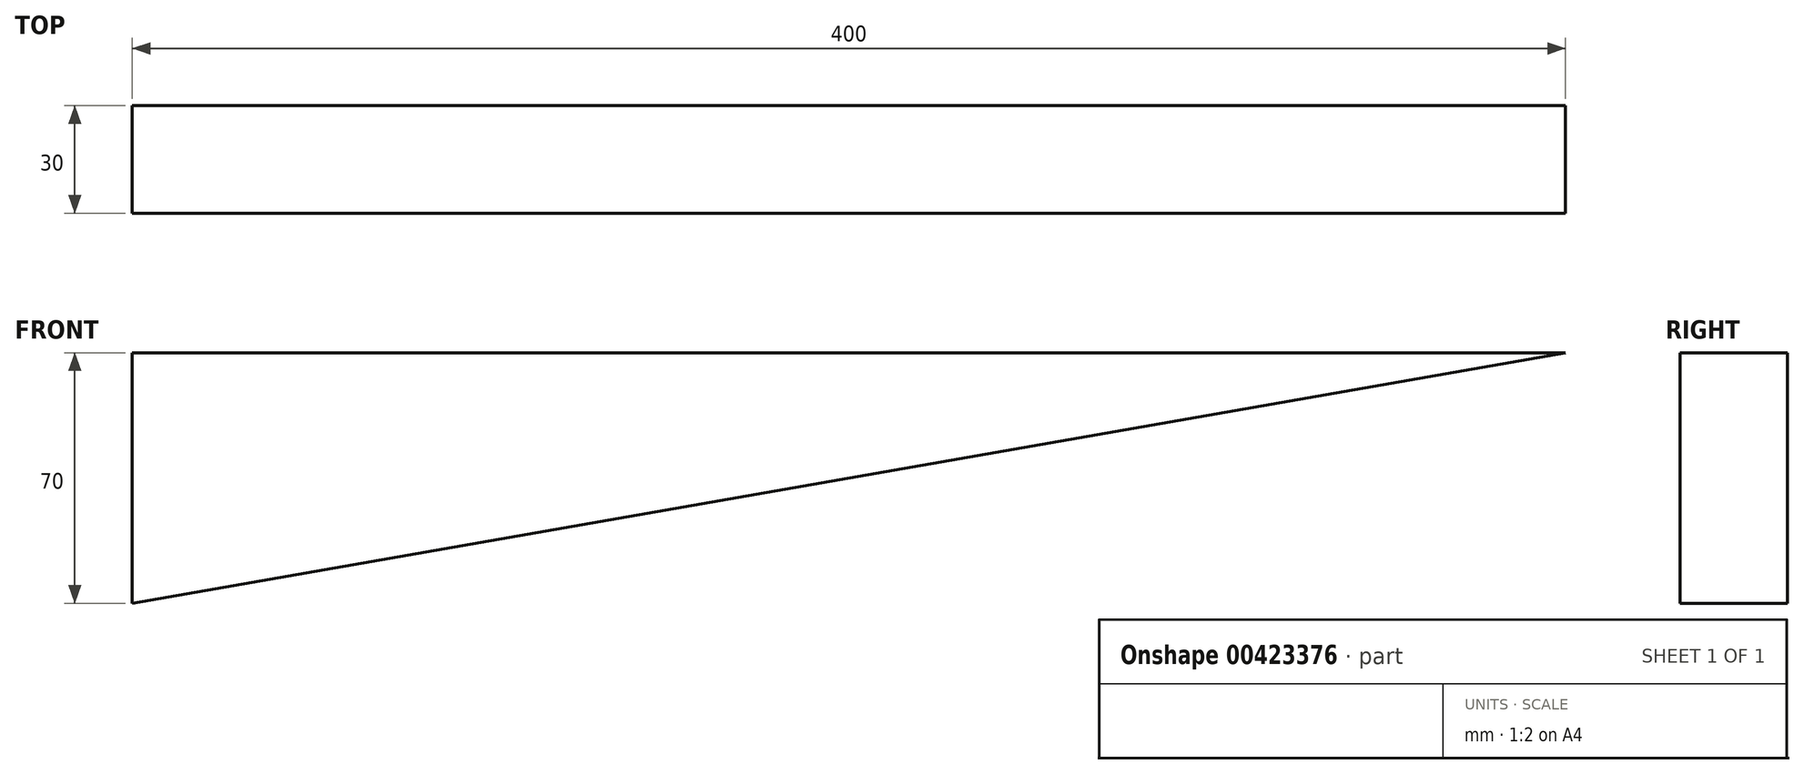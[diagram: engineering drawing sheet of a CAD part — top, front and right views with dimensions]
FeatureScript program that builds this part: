
annotation { "Feature Type Name" : "Feature", "Feature Type Description" : "" }
export const myFeature = defineFeature(function(context is Context, id is Id, definition is map)
    precondition{}
    {
        {
            var Q0;
            Q0=qCreatedBy(makeId("Front.planeOp"),FACE);
            var sketch = newSketch(context, id + "F0", { "sketchPlane" : qUnion([Q0])});
            skLineSegment(sketch, "E0", {"start": v(195.58, -26.53) * mm, "end": v(-204.42, -26.53) * mm});
            skLineSegment(sketch, "E1", {"start": v(-204.42, -26.53) * mm, "end": v(-204.42, -96.53) * mm});
            skLineSegment(sketch, "E2", {"start": v(-204.42, -96.53) * mm, "end": v(195.58, -26.53) * mm});
            skSolve(sketch);
        }
        {
            var Q0;
            Q0=makeQuery(id+"F0.imprint","IMPRINT",FACE,{"disambiguationData":[TD([[makeQuery(id+"F0.imprint","IMPRINT",EDGE,{"derivedFrom":sQuery(id+"F0.wireOp",EDGE,"E0")}),1.0]])]});
            extrude(context, id + "F1", {"entities" : qUnion([Q0]), "depth" : 30 * mm});
        }
    });
